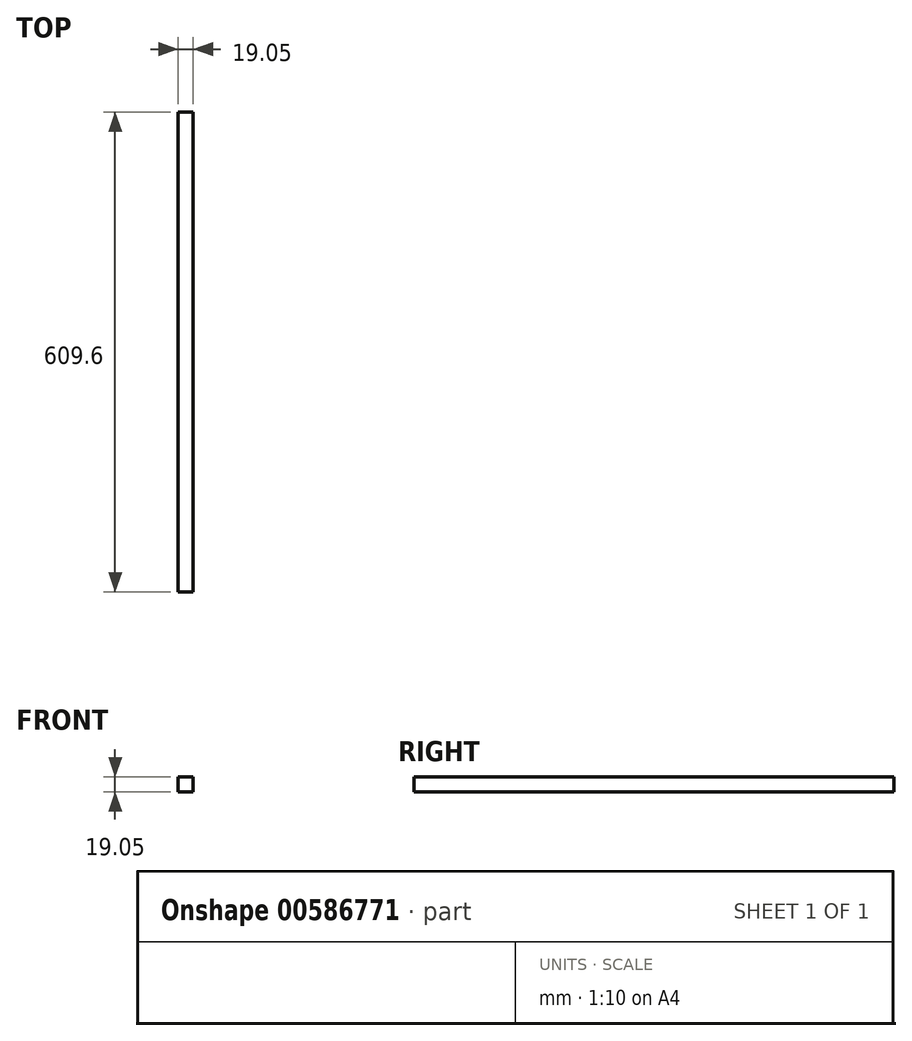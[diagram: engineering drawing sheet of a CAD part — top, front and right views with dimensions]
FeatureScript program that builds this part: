
annotation { "Feature Type Name" : "Feature", "Feature Type Description" : "" }
export const myFeature = defineFeature(function(context is Context, id is Id, definition is map)
    precondition{}
    {
        {
            var Q0;
            Q0=qCreatedBy(makeId("Right.planeOp"),FACE);
            var sketch = newSketch(context, id + "F0", { "sketchPlane" : qUnion([Q0])});
            skLineSegment(sketch, "E0.bottom", {"start": v(-78.28, 7.56) * mm, "end": v(531.32, 7.56) * mm});
            skLineSegment(sketch, "E0.top", {"start": v(-78.28, -11.5) * mm, "end": v(531.32, -11.5) * mm});
            skLineSegment(sketch, "E0.left", {"start": v(-78.28, 7.56) * mm, "end": v(-78.28, -11.5) * mm});
            skLineSegment(sketch, "E0.right", {"start": v(531.32, 7.56) * mm, "end": v(531.32, -11.5) * mm});
            skSolve(sketch);
        }
        {
            var Q0;
            Q0 = qSketchRegion(id + "F0", true);
            extrude(context, id + "F1", {"entities" : qUnion([Q0]), "depth" : 19.05 * mm, "offsetDistance" : 25.4 * mm});
        }
    });
